# Revit family: Electronics_Desono_Biamp_Passive-Subwoofer_SUB2201
name_source: partatom
category: Communication Devices
units: mm (PartAtom-declared; Revit-internal decimal feet)

## family parameters
Cut with Voids When Loaded = No
Host = Face
Maintain Annotation Orientation = No
OmniClass Number = 23.85.10.11.14.14.14
OmniClass Title = Loudspeakers
Part Type = Normal
Room Calculation Point = No
Round Connector Dimension = Use Diameter
Shared = No

## types (1)
- SUB2201
    Connector Description = Speakon™ connector; 49V 250 W 4Ω (1000W peak)
    Continuous Power Handling Nominal Impedance = 49V;250W @ 4Ω (1000W peak)
    Default Elevation = 4' - 0"
    Depth = 1' - 3"
    Description = Desono™ SUB2201 Passive 10 Subwoofer
    Finish = Refer to the Technical Drawings (page 2)
    Height = 1' - 11 1/2"
    Housing Material = Biamp - Plastic - Black
    Input Connection = Speakon™ connector; (2x) 5-way binding posts
    Manufacturer = Biamp
    Model = SUB2201
    Nominal Beamwidth  (H x V) = Omnidirectional
    Nominal Maximum SPL @ 1m = Peak - 120dB; Continuous - 114dB
    Nominal Sensitivity @ 1m = 1W - 96dB; 2.83V - 96dB
    Operating Environment = Indoor
    Operating Mode = Passive
    Operating Range (-3dB) = 45 Hz to 150 Hz
    Product Documentation Link = https://downloads.biamp.com
    Product Page URL = https://www.biamp.com
    Product data url = https://www.bimobject.com
    Recommended Amplifers = 250W - 500W @ 4Ω (49V - 69V)
    Shipping Weight = 43.40 lb
    Transducers = LF 1 x 10 (254 mm) treated paper cone
    URL = https://www.biamp.com
    Weight = 40.79 lb
    Width = 1' - 0"

## geometry (parser evidence)
native form markers: Sweep x2
no freeform markers — native parametric forms only
